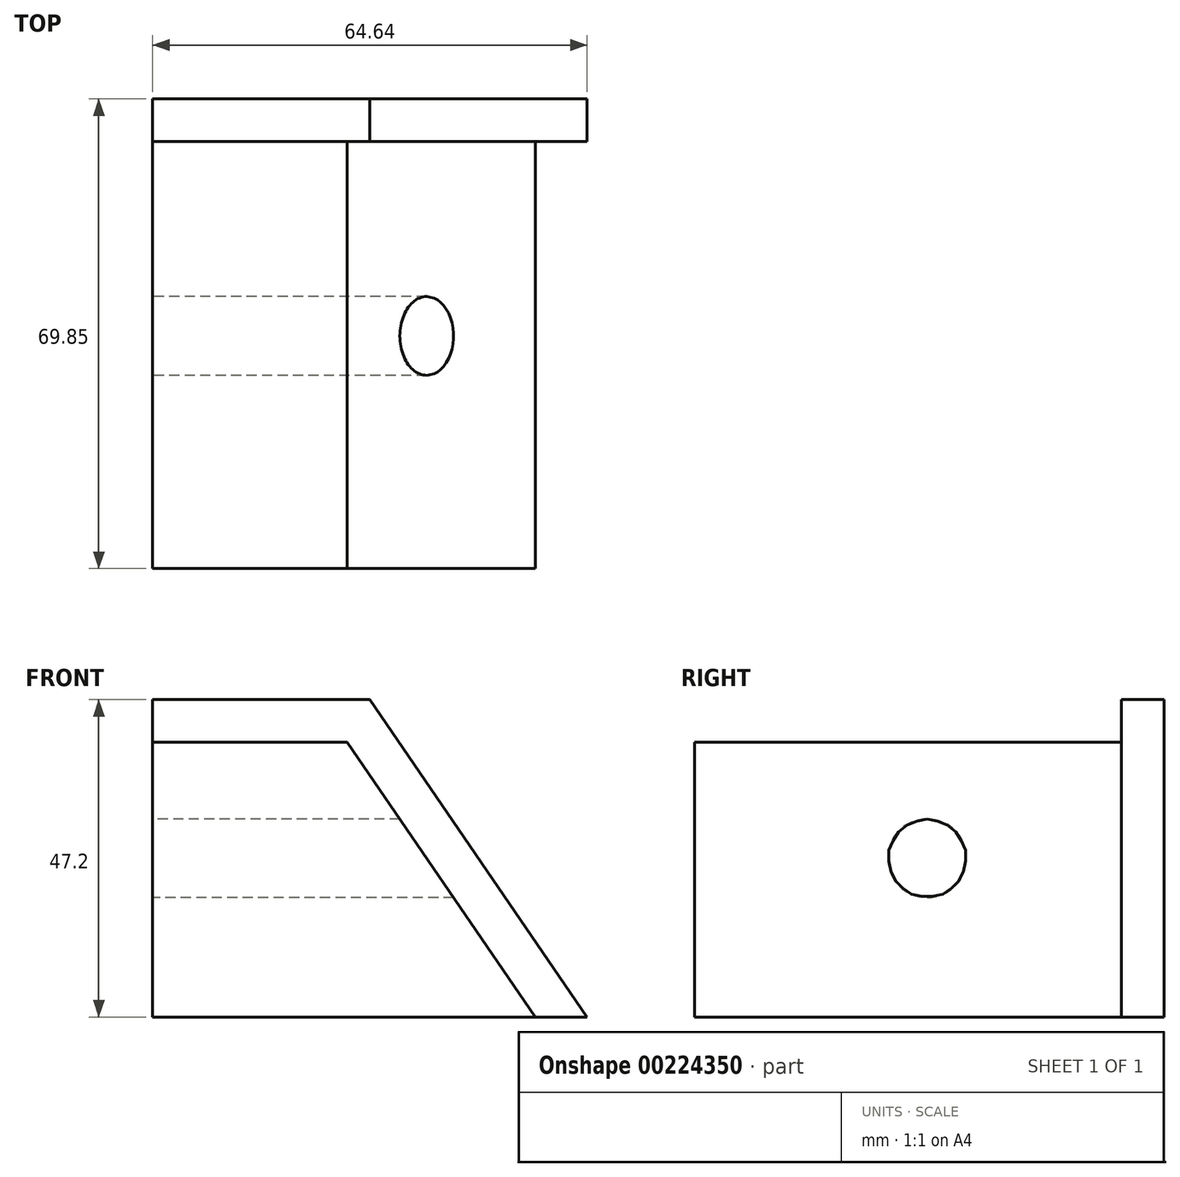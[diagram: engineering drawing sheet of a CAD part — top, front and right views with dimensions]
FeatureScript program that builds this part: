
annotation { "Feature Type Name" : "Feature", "Feature Type Description" : "" }
export const myFeature = defineFeature(function(context is Context, id is Id, definition is map)
    precondition{}
    {
        {
            var Q0;
            Q0=qCreatedBy(makeId("Front.planeOp"),FACE);
            var sketch = newSketch(context, id + "F0", { "sketchPlane" : qUnion([Q0])});
            skLineSegment(sketch, "E0.bottom", {"start": v(-32.32, 23.6) * mm, "end": v(0, 23.6) * mm});
            skLineSegment(sketch, "E0.top", {"start": v(-32.32, -23.6) * mm, "end": v(32.32, -23.6) * mm});
            skLineSegment(sketch, "E0.left", {"start": v(-32.32, 23.6) * mm, "end": v(-32.32, -23.6) * mm});
            skPoint(sketch, "E0.middle", {"position": v(0, 0) * mm});
            skLineSegment(sketch, "E1", {"start": v(0, 23.6) * mm, "end": v(32.32, -23.6) * mm});
            skPoint(sketch, "E0.right.start.orphan", {"position": v(32.32, 23.6) * mm});
            skSolve(sketch);
        }
        {
            var Q0;
            Q0=makeQuery(id+"F0.imprint","IMPRINT",FACE,{"disambiguationData":[TD([[makeQuery(id+"F0.imprint","IMPRINT",EDGE,{"derivedFrom":sQuery(id+"F0.wireOp",EDGE,"E0.bottom")}),-1.0]])]});
            extrude(context, id + "F1", {"entities" : qUnion([Q0]), "depth" : 6.35 * mm});
        }
        {
            var Q0;
            Q0=makeQuery(id+"F1.opExtrude","CAP_FACE",FACE,{"disambiguationData":[OSD([sQuery(id+"F0.wireOp",EDGE,"E0.bottom"),sQuery(id+"F0.wireOp",EDGE,"E0.top"),sQuery(id+"F0.wireOp",EDGE,"E0.left"),sQuery(id+"F0.wireOp",EDGE,"E1")])],"isStart":false});
            var sketch = newSketch(context, id + "F2", { "sketchPlane" : qUnion([Q0])});
            skLineSegment(sketch, "E2", {"start": v(-32.32, 17.25) * mm, "end": v(-3.35, 17.25) * mm});
            skLineSegment(sketch, "E3", {"start": v(-3.35, 17.25) * mm, "end": v(24.62, -23.6) * mm});
            skSolve(sketch);
        }
        {
            var Q0;
            {var subQ0=sQuery(id+"F2.wireOp",EDGE,"E2");Q0=makeQuery(id+"F2.imprint","IMPRINT",FACE,{"disambiguationData":[TD([[makeQuery(id+"F2.imprint","IMPRINT",EDGE,{"derivedFrom":subQ0}),-1.0]])]});}
            extrude(context, id + "F3", {"entities" : qUnion([Q0]), "operationType" : NewBodyOperationType.ADD, "depth" : 63.5 * mm});
        }
        {
            var Q0;
            {var subQ0=sQuery(id+"F0.wireOp",EDGE,"E0.left");Q0=makeQuery(id+"F3.boolean.opBoolean","MERGE",FACE,{"derivedFrom":[makeQuery(id+"F1.opExtrude","SWEPT_FACE",FACE,{"disambiguationData":[OSD([subQ0])]}),makeQuery(id+"F3.opExtrude","SWEPT_FACE",FACE,{"disambiguationData":[OSD([subQ0])]})]});}
            var sketch = newSketch(context, id + "F4", { "sketchPlane" : qUnion([Q0])});
            skCircle(sketch, "E4", {"center": v(35.26, 0) * mm, "radius": 5.86 * mm});
            skSolve(sketch);
        }
        {
            var Q0;
            Q0 = qSketchRegion(id + "F4", true);
            extrude(context, id + "F5", {"entities" : qUnion([Q0]), "operationType" : NewBodyOperationType.REMOVE, "oppositeDirection" : true, "depth" : 99.06 * mm});
        }
    });
